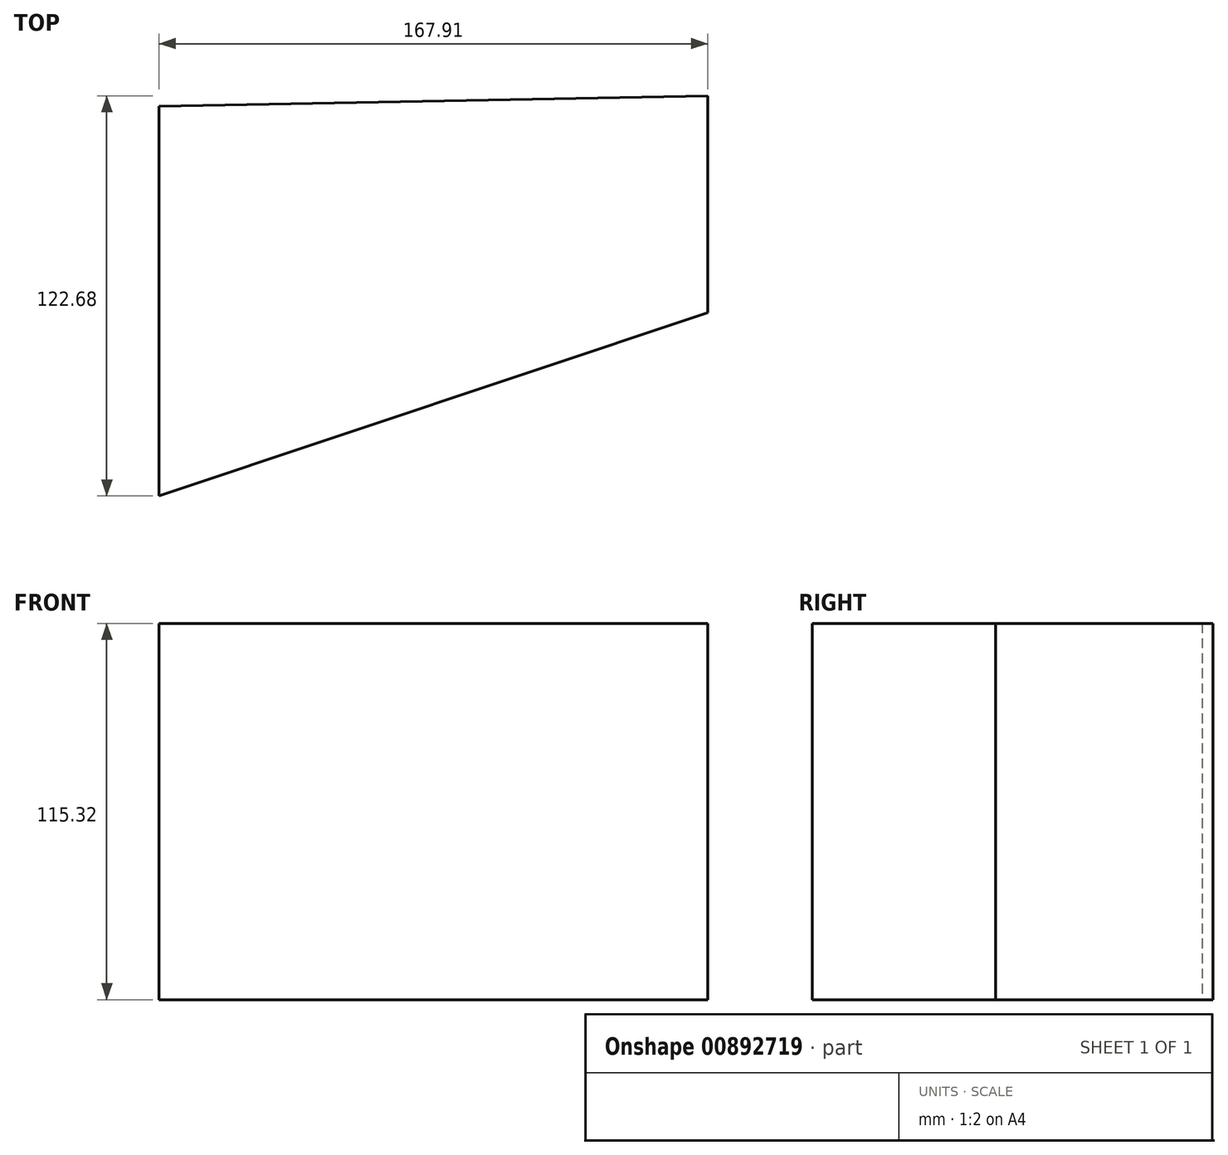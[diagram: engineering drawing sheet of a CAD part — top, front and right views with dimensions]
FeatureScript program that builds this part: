
annotation { "Feature Type Name" : "Feature", "Feature Type Description" : "" }
export const myFeature = defineFeature(function(context is Context, id is Id, definition is map)
    precondition{}
    {
        {
            var Q0;
            Q0=qCreatedBy(makeId("Top.planeOp"),FACE);
            var sketch = newSketch(context, id + "F0", { "sketchPlane" : qUnion([Q0])});
            skLineSegment(sketch, "E0", {"start": v(-119, -158.58) * mm, "end": v(-119, -39.1) * mm});
            skLineSegment(sketch, "E1", {"start": v(-119, -39.1) * mm, "end": v(48.9, -35.9) * mm});
            skLineSegment(sketch, "E2", {"start": v(48.9, -35.9) * mm, "end": v(48.9, -102.37) * mm});
            skLineSegment(sketch, "E3", {"start": v(48.9, -102.37) * mm, "end": v(-119, -158.58) * mm});
            skSolve(sketch);
        }
        {
            var Q0;
            Q0 = qSketchRegion(id + "F0", true);
            extrude(context, id + "F1", {"entities" : qUnion([Q0]), "depth" : 115.32 * mm, "offsetDistance" : 25.4 * mm});
        }
    });
